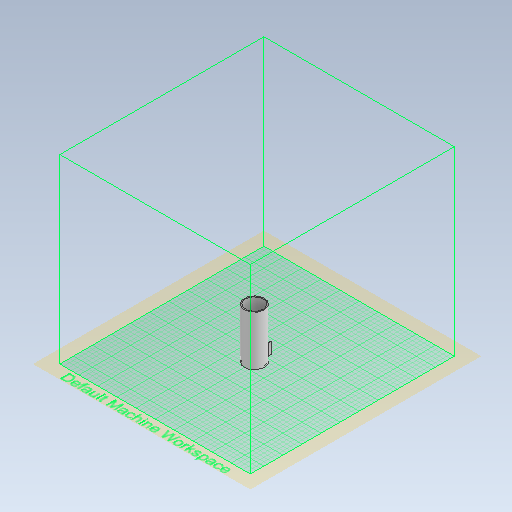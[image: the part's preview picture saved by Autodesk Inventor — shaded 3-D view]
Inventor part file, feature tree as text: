
AUTODESK INVENTOR PART (.ipt)
format: ipt  version: 2021 (Build 250183000, 183)  size: 487,424 bytes
history: native  units: in
note: dims shown in document units (in); Inventor stores cm internally (conversion verified against a paired STEP export)
features: projected_geometry x11, extrude x9, sketch x8, chamfer x4, plane x1, pattern_linear x1
ambient origin geometry x8: Origin, YZ Plane, XZ Plane, XY Plane, X Axis, Y Axis, Z Axis, Center Point
bodies: Solid1 (feature_tree)
feature tree (34):
  extrude  "Extrusion1"  Depth=4.3307in TaperAngle=0.0deg
  plane  "Work Plane1"
  extrude  "Extrusion7"  Depth=4.252in TaperAngle=0.0deg
  extrude  "Extrusion8"  Depth=0.9843in
  extrude  "Extrusion9"  Depth=0.2047in
  extrude  "Extrusion10"  Depth=0.1181in
  extrude  "Extrusion11"  Depth=0.0591in
  extrude  "Extrusion12"  Depth=0.0591in
  pattern_linear  "Rectangular Pattern3"  Spacing1=1.6929in  [1 undecoded]
  extrude  "Extrusion13"  Depth=1.811in
  chamfer  "Chamfer2"  Distance=0.0394in
  chamfer  "Chamfer4"  Distance=0.0098in
  chamfer  "Chamfer5"  Distance=8.2677in
  extrude  "Extrusion14"  Depth=0.248in
  chamfer  "Chamfer6"  Distance=0.3937in
  sketch  "Sketch2"  dims[d2=1.752in d3=4.3307in d4=0.0in]
  sketch  "Sketch9"  dims[d54=1.5748in d55=4.252in d56=0.0in]
  projected_geometry  "Projected Loop7"
  sketch  "Sketch10"  dims[d57=0.3937in d58=0.9843in]
  projected_geometry  "Projected Loop8"
  sketch  "Sketch11"  dims[d59=0.3937in d60=0.0236in d61=0.0in d62=0.0in d63=0.2047in]
  projected_geometry  "Projected Loop9"
  sketch  "Sketch12"  dims[d64=0.126in d65=0.1181in]
  projected_geometry  "Projected Loop10"
  projected_geometry  "Projected Loop11"
  projected_geometry  "Projected Loop12"
  sketch  "Sketch14"  dims[d66=0.0551in d67=0.0in d68=0.0591in]
  projected_geometry  "Projected Loop14"
  projected_geometry  "Projected Loop15"
  sketch  "Sketch16"  dims[d69=0.0591in d70=0.0591in]
  projected_geometry  "Projected Loop16"
  sketch  "Sketch17"  dims[d71=0.9646in d72=0.0in d76=1.6929in d77=0.0in d84=1.811in d85=0.0394in d86=0.0098in d87=0.0in d88=8.2677in d90=0.0787in d92=0.248in d93=0.3937in d94=0.0in d95=0.0787in d96=0.0059in d97=0.0185in d98=0.0787in d99=45.0deg d103=0.1575in d104=0.0787in d105=45.0deg d106=0.0098in d107=0.0787in d108=45.0deg d109=0.5906in d110=0.0315in d111=0.0in d112=0.0315in d113=0.0787in d114=45.0deg d19=0.0197in d20=0.0344in d21=0.0197in d22=0.0344in]
  projected_geometry  "Projected Loop17"
  projected_geometry  "Projected Loop18"
note: 1 required parameter value undecoded (feature->parameter linkage not recoverable at this tier; creation-order binding heuristic only, values carry confidence <= 0.55)
